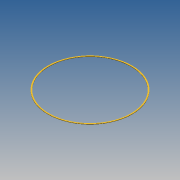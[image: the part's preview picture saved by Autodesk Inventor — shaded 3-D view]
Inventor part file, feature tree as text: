
AUTODESK INVENTOR PART (.ipt)
format: ipt  version: 2014 SP1 (Build 180222100, 222)  size: 75,776 bytes
history: native  units: in
note: dims shown in document units (in); Inventor stores cm internally (conversion verified against a paired STEP export)
features: extrude x1, sketch x1
ambient origin geometry x8: Origin, YZ Plane, XZ Plane, XY Plane, X Axis, Y Axis, Z Axis, Center Point
bodies: Solid1 (feature_tree)
feature tree (2):
  extrude  "Extrusion1"  Depth=0.1in
  sketch  "Sketch1"  dims[d0=18.0in d1=0.25in d2=0.1in d3=0.0in]
